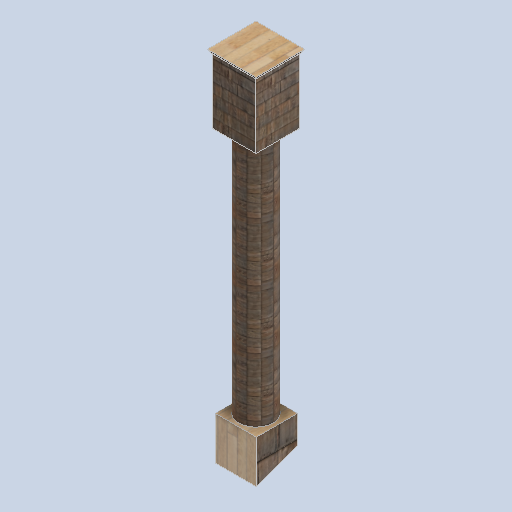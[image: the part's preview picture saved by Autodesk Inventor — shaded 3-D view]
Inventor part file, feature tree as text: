
AUTODESK INVENTOR PART (.ipt)
format: ipt  version: 2024.2 (Build 282272000, 272)  size: 176,128 bytes
history: native  units: in
note: dims shown in document units (in); Inventor stores cm internally (conversion verified against a paired STEP export)
features: sketch x5, other x3, plane x1
ambient origin geometry x8: Origin, YZ Plane, XZ Plane, XY Plane, X Axis, Y Axis, Z Axis, Center Point
bodies: Solid1 (feature_tree)
feature tree (9):
  other  "side_pillar_01.ipt"
  other  "Solid1::side_pillar_01.ipt"
  other  "TaggingFeature1"
  sketch  "Sketch1"  dims[d0=0.3937in]
  sketch  "Sketch2"
  sketch  "Sketch3"
  sketch  "Sketch4"
  sketch  "Sketch5"
  plane  "Work Plane3"
